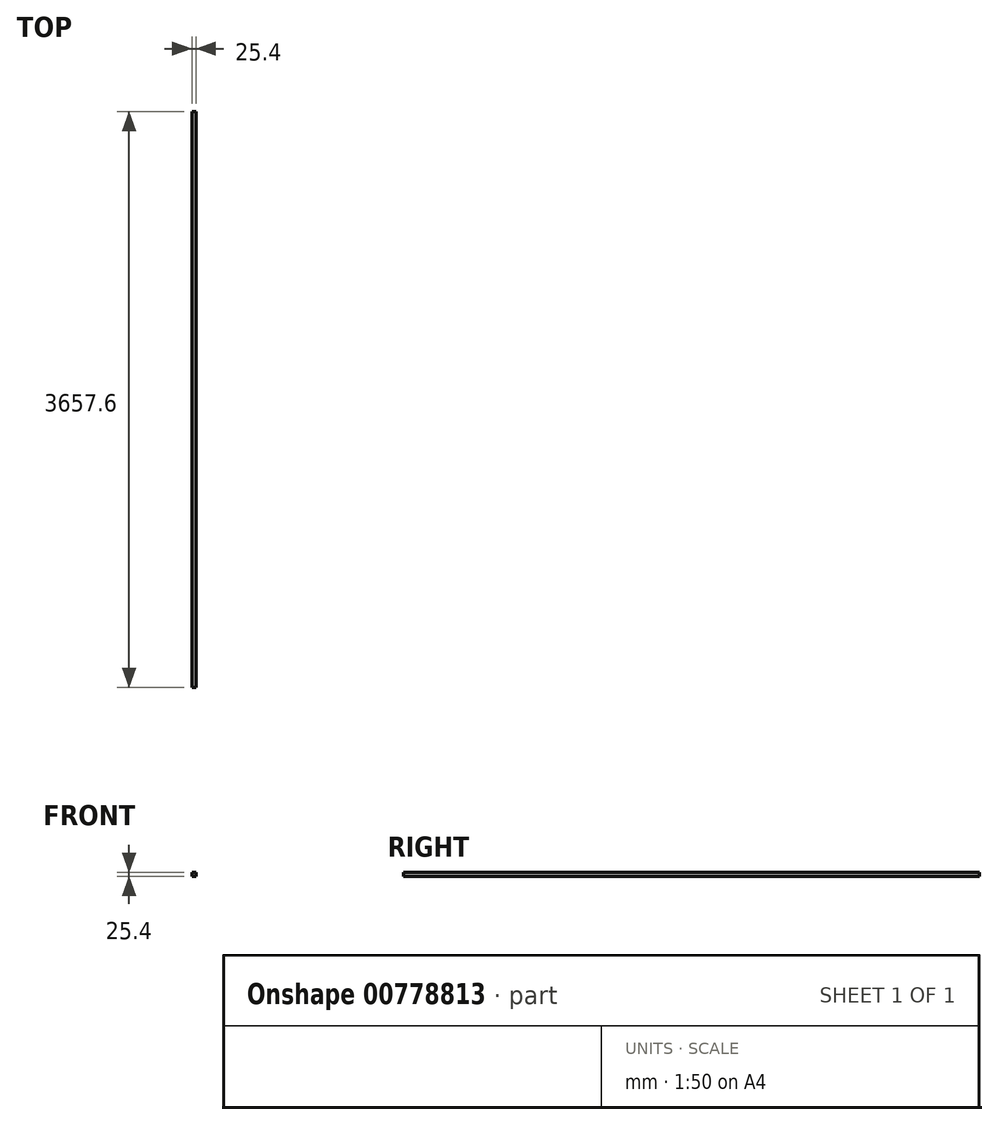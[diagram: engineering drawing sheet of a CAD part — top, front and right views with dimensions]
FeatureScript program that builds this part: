
annotation { "Feature Type Name" : "Feature", "Feature Type Description" : "" }
export const myFeature = defineFeature(function(context is Context, id is Id, definition is map)
    precondition{}
    {
        {
            var Q0;
            Q0=qCreatedBy(makeId("Front.planeOp"),FACE);
            var sketch = newSketch(context, id + "F0", { "sketchPlane" : qUnion([Q0])});
            skLineSegment(sketch, "E0.bottom", {"start": v(0, 0) * mm, "end": v(25.4, 0) * mm});
            skLineSegment(sketch, "E0.top", {"start": v(0, 25.4) * mm, "end": v(25.4, 25.4) * mm});
            skLineSegment(sketch, "E0.left", {"start": v(0, 0) * mm, "end": v(0, 25.4) * mm});
            skLineSegment(sketch, "E0.right", {"start": v(25.4, 0) * mm, "end": v(25.4, 25.4) * mm});
            skSolve(sketch);
        }
        {
            var Q0;
            Q0=makeQuery(id+"F0.imprint","IMPRINT",FACE,{"disambiguationData":[TD([[makeQuery(id+"F0.imprint","IMPRINT",EDGE,{"derivedFrom":sQuery(id+"F0.wireOp",EDGE,"E0.bottom")}),1.0]])]});
            extrude(context, id + "F1", {"entities" : qUnion([Q0]), "depth" : 3657.6 * mm, "offsetDistance" : 25.4 * mm});
        }
    });
